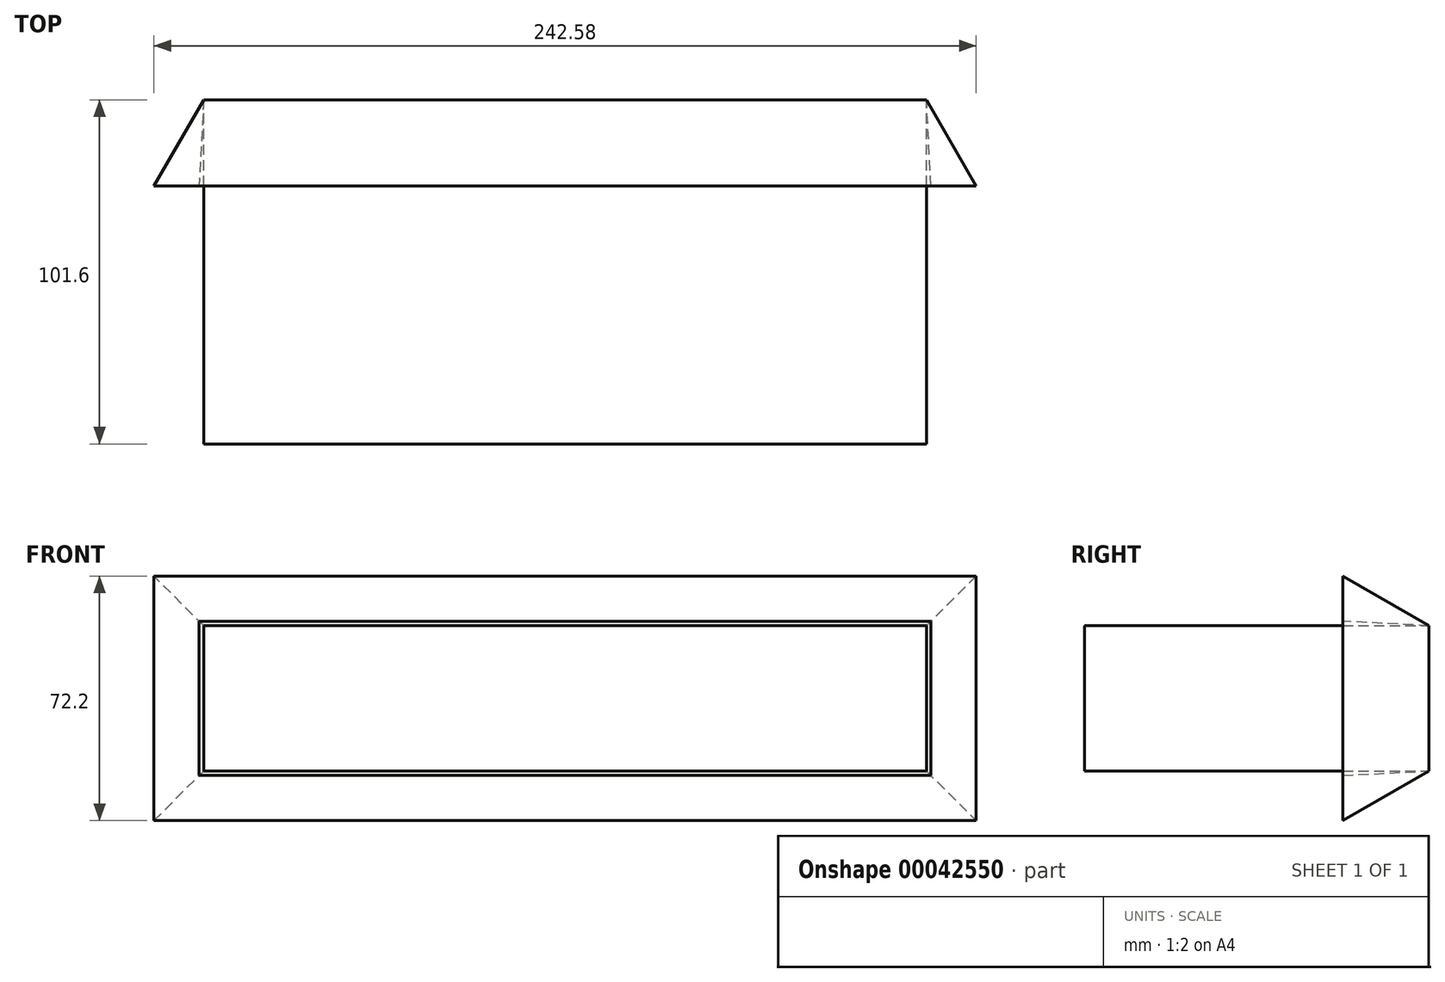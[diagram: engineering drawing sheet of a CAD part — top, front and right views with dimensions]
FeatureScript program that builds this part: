
annotation { "Feature Type Name" : "Feature", "Feature Type Description" : "" }
export const myFeature = defineFeature(function(context is Context, id is Id, definition is map)
    precondition{}
    {
        {
            var Q0;
            Q0=qCreatedBy(makeId("Front.planeOp"),FACE);
            var sketch = newSketch(context, id + "F0", { "sketchPlane" : qUnion([Q0])});
            skLineSegment(sketch, "E0.bottom", {"start": v(-92.2, 36.1) * mm, "end": v(121.04, 36.1) * mm});
            skLineSegment(sketch, "E0.top", {"start": v(-92.2, -6.79) * mm, "end": v(121.04, -6.79) * mm});
            skLineSegment(sketch, "E0.left", {"start": v(-92.2, 36.1) * mm, "end": v(-92.2, -6.79) * mm});
            skLineSegment(sketch, "E0.right", {"start": v(121.04, 36.1) * mm, "end": v(121.04, -6.79) * mm});
            skSolve(sketch);
        }
        {
            var Q0;
            Q0 = qSketchRegion(id + "F0", true);
            extrude(context, id + "F1", {"entities" : qUnion([Q0]), "depth" : 25.4 * mm, "hasDraft" : true, "draftAngle" : 30 * degree});
        }
        {
            var Q0;
            Q0 = qSketchRegion(id + "F0", true);
            extrude(context, id + "F2", {"entities" : qUnion([Q0]), "depth" : 25.4 * mm, "hasDraft" : true, "draftAngle" : 3 * degree});
        }
        {
            var Q0;
            Q0 = qSketchRegion(id + "F0", true);
            extrude(context, id + "F3", {"entities" : qUnion([Q0]), "depth" : 101.6 * mm});
        }
    });
